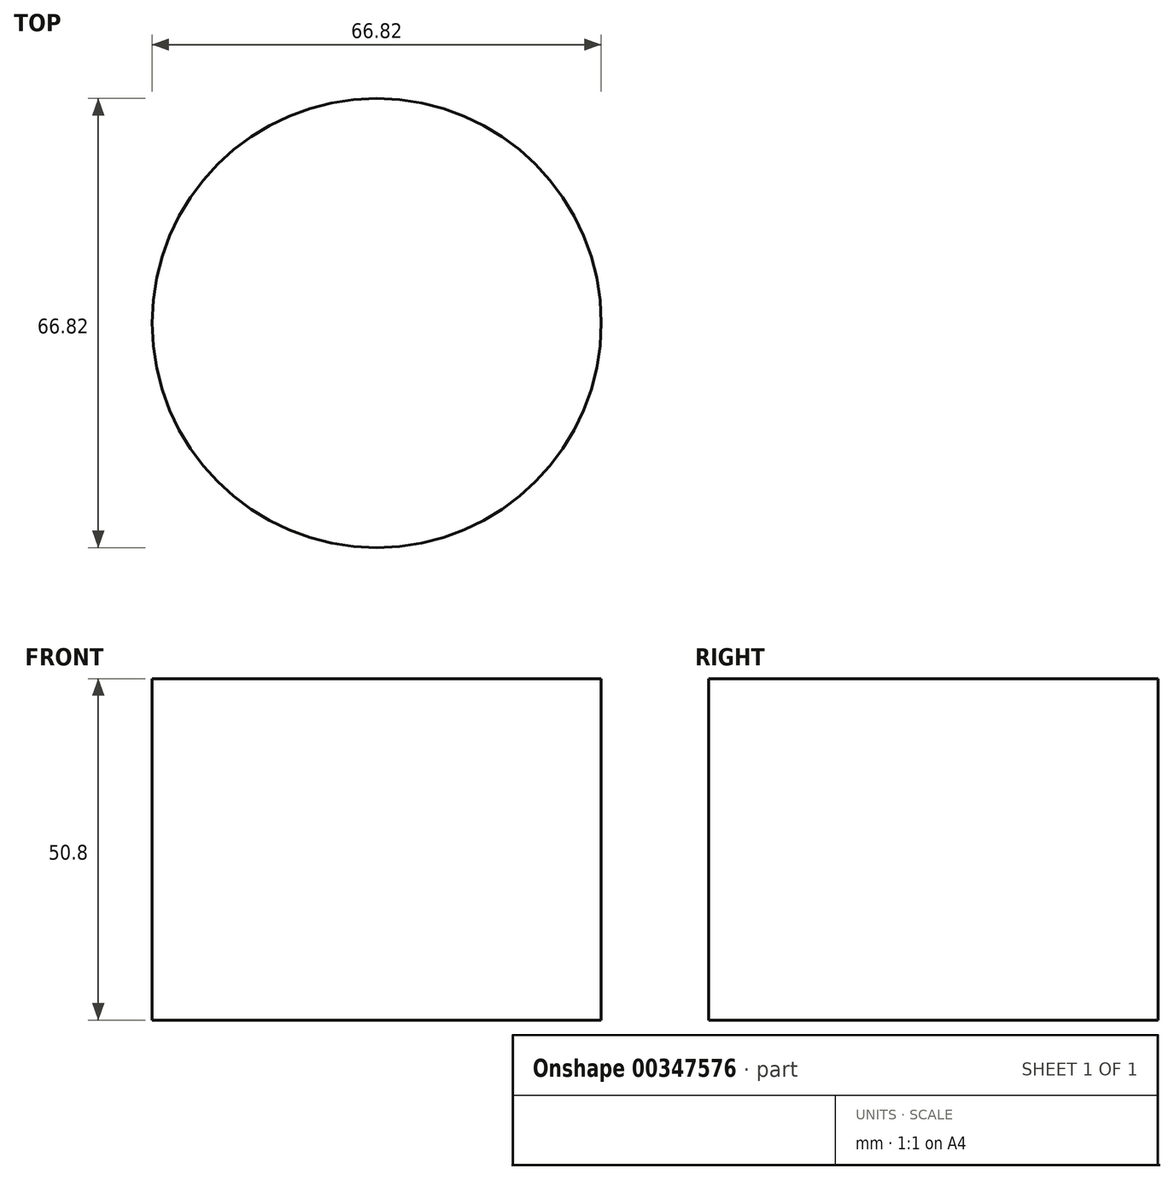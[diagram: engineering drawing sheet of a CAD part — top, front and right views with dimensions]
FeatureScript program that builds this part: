
annotation { "Feature Type Name" : "Feature", "Feature Type Description" : "" }
export const myFeature = defineFeature(function(context is Context, id is Id, definition is map)
    precondition{}
    {
        {
            var Q0;
            Q0=qCreatedBy(makeId("Top.planeOp"),FACE);
            var sketch = newSketch(context, id + "F0", { "sketchPlane" : qUnion([Q0])});
            skCircle(sketch, "E0", {"center": v(0, 0) * mm, "radius": 33.41 * mm});
            skSolve(sketch);
        }
        {
            var Q0;
            Q0=makeQuery(id+"F0.imprint","IMPRINT",FACE,{"disambiguationData":[TD([[makeQuery(id+"F0.imprint","IMPRINT",EDGE,{"derivedFrom":sQuery(id+"F0.wireOp",EDGE,"E0")}),1.0]])]});
            extrude(context, id + "F1", {"entities" : qUnion([Q0]), "depth" : 50.8 * mm});
        }
    });
